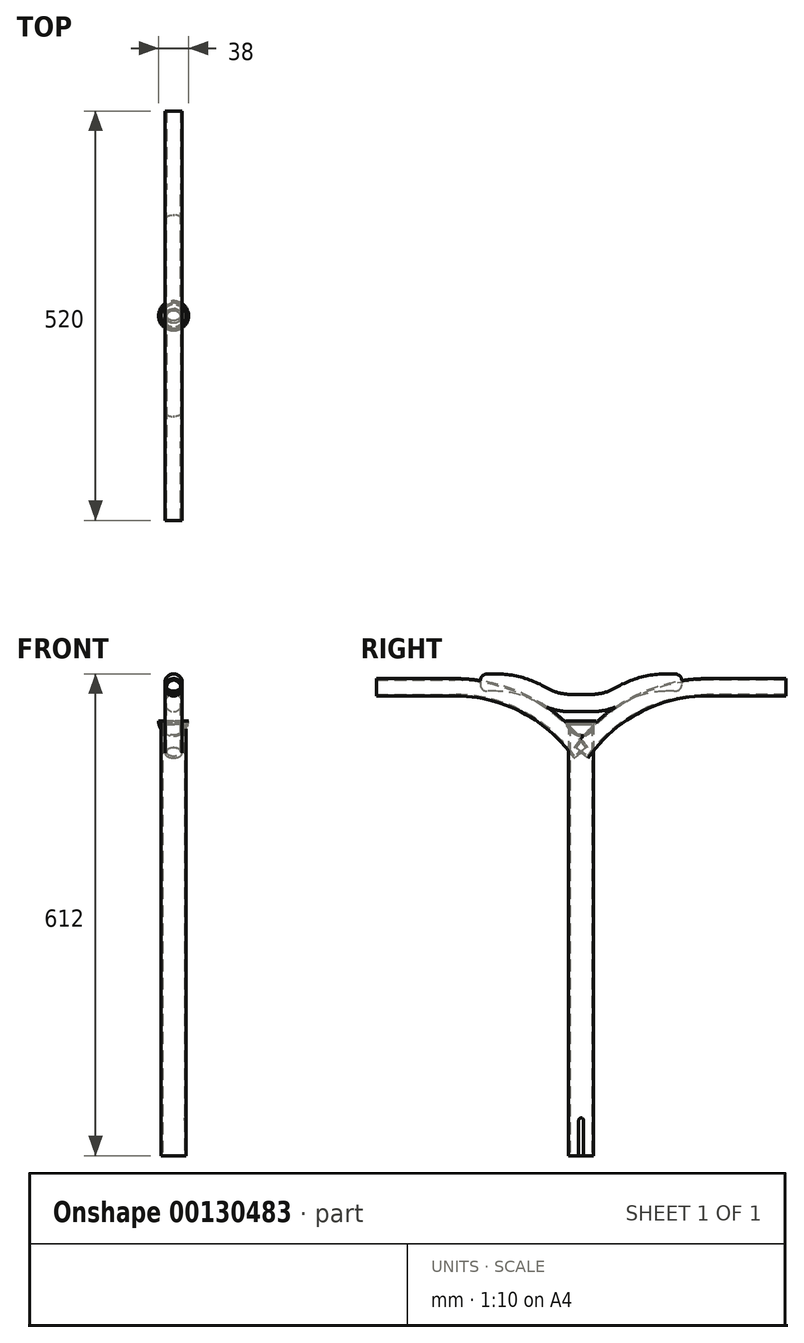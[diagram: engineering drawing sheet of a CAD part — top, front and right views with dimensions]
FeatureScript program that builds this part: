
annotation { "Feature Type Name" : "Feature", "Feature Type Description" : "" }
export const myFeature = defineFeature(function(context is Context, id is Id, definition is map)
    precondition{}
    {
        {
            var Q0;
            Q0=qCreatedBy(makeId("Top.planeOp"),FACE);
            var sketch = newSketch(context, id + "F0", { "sketchPlane" : qUnion([Q0])});
            skCircle(sketch, "E0", {"center": v(0, 0) * mm, "radius": 16 * mm});
            skSolve(sketch);
        }
        {
            var Q0;
            Q0 = qSketchRegion(id + "F0", true);
            extrude(context, id + "F1", {"entities" : qUnion([Q0]), "depth" : 550 * mm});
        }
        {
            var Q0;
            Q0=makeQuery(id+"F1.opExtrude","CAP_FACE",FACE,{"disambiguationData":[OSD([sQuery(id+"F0.wireOp",EDGE,"E0")])],"isStart":true});
            shell(context, id + "F2", {"entities" : qUnion([Q0]), "thickness" : 2 * mm});
        }
        {
            var Q0;
            Q0=qCreatedBy(makeId("Right.planeOp"),FACE);
            var sketch = newSketch(context, id + "F3", { "sketchPlane" : qUnion([Q0])});
            skLineSegment(sketch, "E1.bottom", {"start": v(-3, 0) * mm, "end": v(3, 0) * mm});
            skLineSegment(sketch, "E1.left", {"start": v(-3, 0) * mm, "end": v(-3, 45) * mm});
            skLineSegment(sketch, "E1.right", {"start": v(3, 0) * mm, "end": v(3, 45) * mm});
            skArc(sketch, "E2", {"start": v(3, 45) * mm, "mid": v(0, 48) * mm, "end": v(-3, 45) * mm});
            skSolve(sketch);
        }
        {
            var Q0;
            Q0=makeQuery(id+"F3.imprint","IMPRINT",FACE,{"disambiguationData":[TD([[makeQuery(id+"F3.imprint","IMPRINT",EDGE,{"derivedFrom":sQuery(id+"F3.wireOp",EDGE,"E1.bottom")}),1.0]])]});
            extrude(context, id + "F4", {"entities" : qUnion([Q0]), "operationType" : NewBodyOperationType.REMOVE, "endBound" : BoundingType.THROUGH_ALL, "depth" : 25 * mm});
        }
        {
            var Q0;
            Q0=qCreatedBy(makeId("Right.planeOp"),FACE);
            var sketch = newSketch(context, id + "F5", { "sketchPlane" : qUnion([Q0])});
            skArc(sketch, "E3", {"start": v(160, 595) * mm, "mid": v(69.75, 572.86) * mm, "end": v(0, 511.47) * mm});
            skLineSegment(sketch, "E4", {"start": v(160, 595) * mm, "end": v(260, 595) * mm});
            skSolve(sketch);
        }
        {
            var Q0;
            Q0=qCreatedBy(makeId("Front.planeOp"),FACE);
            var Q1;
            Q1=sQuery(id+"F5.wireOp",VERTEX,"E4.end");
            cPlane(context, id + "F6", {"entities" : qUnion([Q0, Q1]), "cplaneType" : CPlaneType.PLANE_POINT, "offset" : 25 * mm, "width" : 150 * mm, "height" : 150 * mm});
        }
        {
            var Q0;
            Q0=qCreatedBy(id+"F6.planeOp",FACE);
            var sketch = newSketch(context, id + "F7", { "sketchPlane" : qUnion([Q0])});
            skCircle(sketch, "E5", {"center": v(0, 595) * mm, "radius": 11 * mm});
            skSolve(sketch);
        }
        {
            var Q0;
            Q0=makeQuery(id+"F7.imprint","IMPRINT",FACE,{"disambiguationData":[TD([[makeQuery(id+"F7.imprint","IMPRINT",EDGE,{"derivedFrom":sQuery(id+"F7.wireOp",EDGE,"E5")}),1.0]])]});
            var Q1;
            Q1=sQuery(id+"F5.wireOp",EDGE,"E3");
            var Q2;
            Q2=sQuery(id+"F5.wireOp",EDGE,"E4");
            sweep(context, id + "F8", {"profiles" : qUnion([Q0]), "path" : qUnion([Q1, Q2])});
        }
        {
            var Q0;
            Q0=makeQuery(id+"F8.opSweep","CAP_FACE",FACE,{"disambiguationData":[OSD([sQuery(id+"F5.wireOp",VERTEX,"E4.end"),sQuery(id+"F7.wireOp",EDGE,"E5")])],"isStart":true});
            shell(context, id + "F9", {"entities" : qUnion([Q0]), "thickness" : 2 * mm});
        }
        {
            var Q0;
            Q0=makeQuery(id+"F8.opSweep","SWEPT_BODY",BODY,{"disambiguationData":[OSD([sQuery(id+"F5.wireOp",EDGE,"E4"),sQuery(id+"F7.wireOp",EDGE,"E5")])]});
            var Q1;
            Q1=qCreatedBy(makeId("Front.planeOp"),FACE);
            mirror(context, id + "F10", {"entities" : qUnion([Q0]), "mirrorPlane" : qUnion([Q1])});
        }
        {
            var Q0;
            Q0=qCreatedBy(makeId("Right.planeOp"),FACE);
            var sketch = newSketch(context, id + "F11", { "sketchPlane" : qUnion([Q0])});
            skLineSegment(sketch, "E6", {"start": v(0, 0) * mm, "end": v(0, 700) * mm, "construction": true});
            skLineSegment(sketch, "E7", {"start": v(0, 575) * mm, "end": v(-12.5, 575) * mm});
            skArc(sketch, "E8", {"start": v(-50.21, 585.27) * mm, "mid": v(-32.04, 577.61) * mm, "end": v(-12.5, 575) * mm});
            skArc(sketch, "E9", {"start": v(-50.21, 585.27) * mm, "mid": v(-78.05, 597) * mm, "end": v(-108, 601) * mm});
            skLineSegment(sketch, "E10", {"start": v(-108, 601) * mm, "end": v(-128, 601) * mm});
            skLineSegment(sketch, "E11.MirrorCS", {"start": v(0, 575) * mm, "end": v(12.5, 575) * mm});
            skArc(sketch, "E12.MirrorCS", {"start": v(50.21, 585.27) * mm, "mid": v(32.04, 577.61) * mm, "end": v(12.5, 575) * mm});
            skArc(sketch, "E13.MirrorCS", {"start": v(50.21, 585.27) * mm, "mid": v(78.05, 597) * mm, "end": v(108, 601) * mm});
            skLineSegment(sketch, "E14.MirrorCS", {"start": v(108, 601) * mm, "end": v(128, 601) * mm});
            skSolve(sketch);
        }
        {
            var Q0;
            Q0=sQuery(id+"F11.wireOp",VERTEX,"E14.MirrorCS.end");
            var Q1;
            Q1=qCreatedBy(id+"F6.planeOp",FACE);
            cPlane(context, id + "F12", {"entities" : qUnion([Q0, Q1]), "cplaneType" : CPlaneType.PLANE_POINT, "offset" : 25 * mm, "width" : 150 * mm, "height" : 150 * mm});
        }
        {
            var Q0;
            Q0=qCreatedBy(id+"F12.planeOp",FACE);
            var sketch = newSketch(context, id + "F13", { "sketchPlane" : qUnion([Q0])});
            skCircle(sketch, "E15", {"center": v(0, 601) * mm, "radius": 11 * mm});
            skSolve(sketch);
        }
        {
            var Q0;
            Q0=makeQuery(id+"F13.imprint","IMPRINT",FACE,{"disambiguationData":[TD([[makeQuery(id+"F13.imprint","IMPRINT",EDGE,{"derivedFrom":sQuery(id+"F13.wireOp",EDGE,"E15")}),1.0]])]});
            var Q1;
            Q1=sQuery(id+"F11.wireOp",EDGE,"E14.MirrorCS");
            var Q2;
            Q2=sQuery(id+"F11.wireOp",EDGE,"E10");
            var Q3;
            Q3=sQuery(id+"F11.wireOp",EDGE,"E9");
            var Q4;
            Q4=sQuery(id+"F11.wireOp",EDGE,"E13.MirrorCS");
            var Q5;
            Q5=sQuery(id+"F11.wireOp",EDGE,"E12.MirrorCS");
            var Q6;
            Q6=sQuery(id+"F11.wireOp",EDGE,"E8");
            var Q7;
            Q7=sQuery(id+"F11.wireOp",EDGE,"E11.MirrorCS");
            var Q8;
            Q8=sQuery(id+"F11.wireOp",EDGE,"E7");
            sweep(context, id + "F14", {"profiles" : qUnion([Q0]), "path" : qUnion([Q1, Q2, Q3, Q4, Q5, Q6, Q7, Q8])});
        }
        {
            var Q0;
            Q0=makeQuery(id+"F14.opSweep","CAP_FACE",FACE,{"disambiguationData":[OSD([sQuery(id+"F11.wireOp",VERTEX,"E14.MirrorCS.end"),sQuery(id+"F13.wireOp",EDGE,"E15")])],"isStart":true});
            var Q1;
            Q1=makeQuery(id+"F14.opSweep","CAP_FACE",FACE,{"disambiguationData":[OSD([sQuery(id+"F11.wireOp",VERTEX,"E10.end"),sQuery(id+"F13.wireOp",EDGE,"E15")])],"isStart":false});
            fillet(context, id + "F15", {"entities" : qUnion([Q0, Q1]), "radius" : 10 * mm, "tangentPropagation" : true, "rho" : 0.5, "crossSection" : FilletCrossSection.CONIC, "allowEdgeOverflow" : false});
        }
        {
            var Q0;
            Q0=qCreatedBy(makeId("Right.planeOp"),FACE);
            var sketch = newSketch(context, id + "F16", { "sketchPlane" : qUnion([Q0])});
            skArc(sketch, "E16", {"start": v(-19, 552) * mm, "mid": v(-13.44, 538.56) * mm, "end": v(0, 533) * mm});
            skLineSegment(sketch, "E17", {"start": v(-19, 552) * mm, "end": v(0, 552) * mm});
            skLineSegment(sketch, "E18", {"start": v(0, 552) * mm, "end": v(0, 533) * mm});
            skSolve(sketch);
        }
        {
            var Q0;
            Q0 = qSketchRegion(id + "F16", true);
            var Q1;
            Q1=sQuery(id+"F16.wireOp",EDGE,"E18");
            revolve(context, id + "F17", {"entities" : qUnion([Q0]), "axis" : qUnion([Q1]), "revolveType" : RevolveType.FULL});
        }
        {
            var Q0;
            Q0=makeQuery(id+"F17.opRevolve","SWEPT_FACE",FACE,{"disambiguationData":[OSD([sQuery(id+"F16.wireOp",EDGE,"E17")])]});
            shell(context, id + "F18", {"entities" : qUnion([Q0]), "thickness" : 2 * mm});
        }
    });
